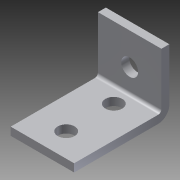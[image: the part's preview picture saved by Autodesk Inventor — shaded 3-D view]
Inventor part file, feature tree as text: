
AUTODESK INVENTOR PART (.ipt)
format: ipt  version: 2014 SP1 (Build 180222100, 222)  size: 168,960 bytes
history: native  units: in
note: dims shown in document units (in); Inventor stores cm internally (conversion verified against a paired STEP export)
features: other x4, sheet_metal_op x3, sketch x3
ambient origin geometry x8: Origin, YZ Plane, XZ Plane, XY Plane, X Axis, Y Axis, Z Axis, Center Point
bodies: Solid1 (feature_tree)
feature tree (10):
  sheet_metal_op  "Face1"
  sheet_metal_op  "Flange1"
  sketch  "Sketch1"  dims[d0=1.0in]
  other  "Plate1"
  sketch  "Sketch2"  dims[d1=1.5in]
  other  "Plate2"
  sheet_metal_op  "Bend1"
  sketch  "Sketch3"  dims[d2=0.266in d3=0.266in d4=0.375in d5=0.375in d6=0.5in d7=0.5in d8=0.125in d9=0.125in d10=0.0625in d11=0.25in d12=0.125in d13=1.0in d14=90.0deg d15=0.05in d16=0.5in d17=0.125in d18=0.125in d19=0.266in d20=0.5in d21=0.5in d22=0.125in d23=0.0in]
  other  "Cut1"
  other  "Definition1"
